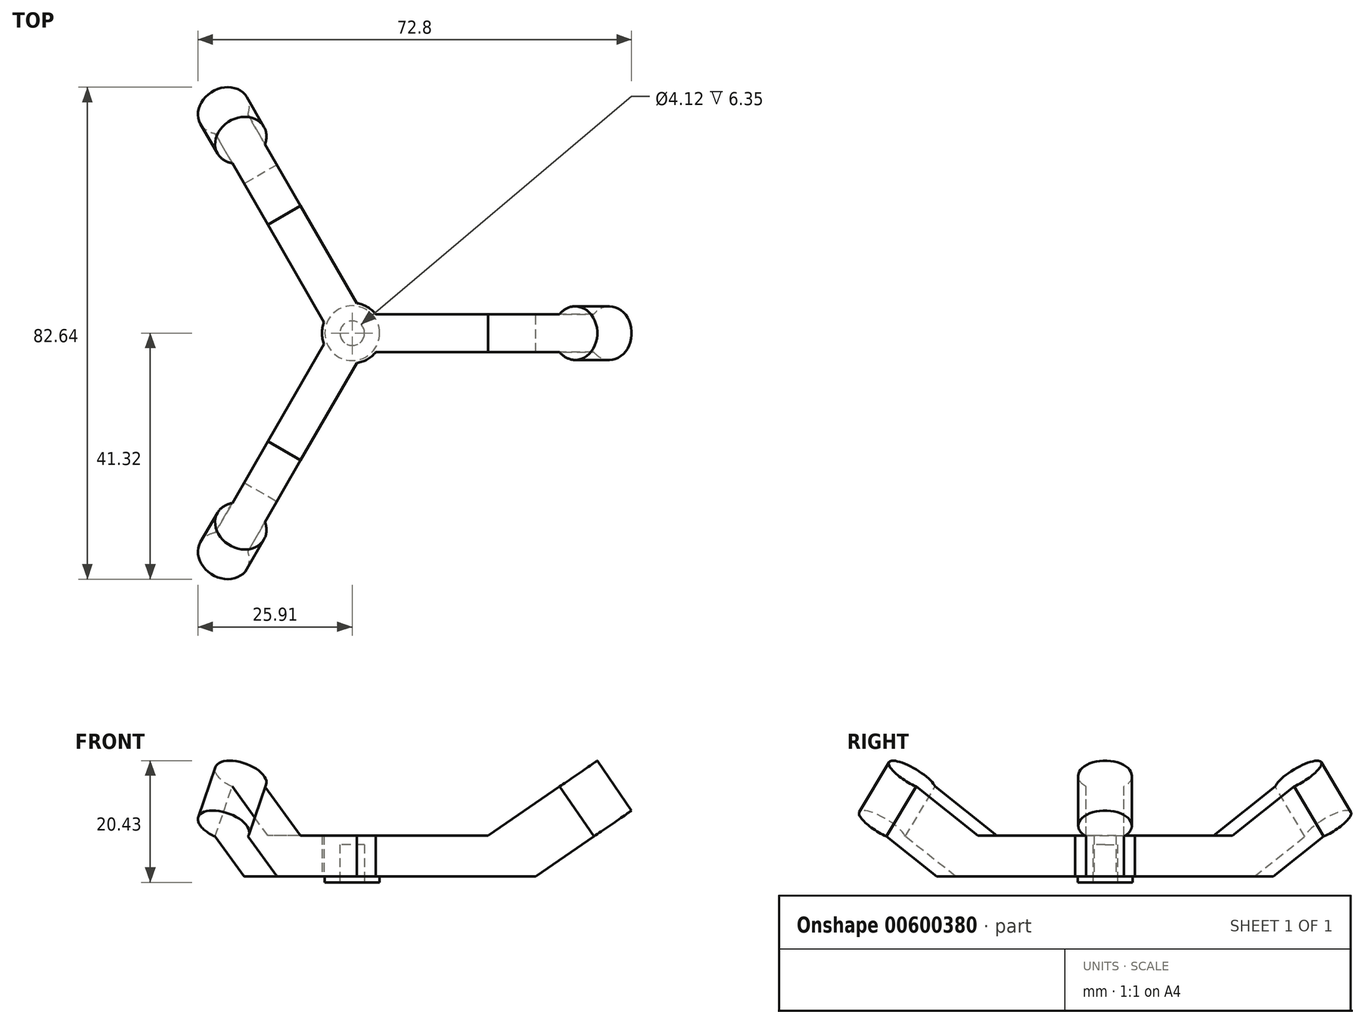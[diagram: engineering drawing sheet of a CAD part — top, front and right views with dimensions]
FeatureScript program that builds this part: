
annotation { "Feature Type Name" : "Feature", "Feature Type Description" : "" }
export const myFeature = defineFeature(function(context is Context, id is Id, definition is map)
    precondition{}
    {
        {
            var Q0;
            Q0=qCreatedBy(makeId("Front.planeOp"),FACE);
            var sketch = newSketch(context, id + "F0", { "sketchPlane" : qUnion([Q0])});
            skCircle(sketch, "E0", {"center": v(0, 59.06) * mm, "radius": 63.5 * mm, "construction": true});
            skCircle(sketch, "E1", {"center": v(38.1, 3.57) * mm, "radius": 5 * mm, "construction": true});
            skLineSegment(sketch, "E2", {"start": v(33.16, 2.82) * mm, "end": v(40.58, 7.9) * mm, "construction": true});
            skLineSegment(sketch, "E3", {"start": v(33.16, 2.82) * mm, "end": v(33.72, 2) * mm, "construction": true});
            skLineSegment(sketch, "E4", {"start": v(33.72, 2) * mm, "end": v(41.14, 7.09) * mm, "construction": true});
            skLineSegment(sketch, "E5", {"start": v(41.14, 7.09) * mm, "end": v(40.58, 7.9) * mm, "construction": true});
            skLineSegment(sketch, "E6", {"start": v(38.1, 3.57) * mm, "end": v(0, 59.06) * mm, "construction": true});
            skLineSegment(sketch, "E7", {"start": v(0, -6.99) * mm, "end": v(2.06, -6.99) * mm});
            skLineSegment(sketch, "E8", {"start": v(2.06, -6.99) * mm, "end": v(2.06, -12.34) * mm});
            skLineSegment(sketch, "E9", {"start": v(0, -6.99) * mm, "end": v(0, -5.49) * mm});
            skLineSegment(sketch, "E10", {"start": v(0, -5.49) * mm, "end": v(22.83, -5.49) * mm});
            skLineSegment(sketch, "E11", {"start": v(22.83, -5.49) * mm, "end": v(33.72, 2) * mm});
            skLineSegment(sketch, "E12", {"start": v(33.72, 2) * mm, "end": v(41.14, 7.09) * mm});
            skLineSegment(sketch, "E13", {"start": v(2.06, -12.34) * mm, "end": v(30.8, -12.33) * mm});
            skLineSegment(sketch, "E14", {"start": v(30.8, -12.33) * mm, "end": v(46.9, -1.3) * mm});
            skLineSegment(sketch, "E15", {"start": v(46.9, -1.3) * mm, "end": v(41.14, 7.09) * mm});
            skLineSegment(sketch, "E16", {"start": v(0, 0) * mm, "end": v(0, -5.49) * mm, "construction": true});
            skSolve(sketch);
        }
        {
            var Q0;
            Q0=qSketchRegion(id+"F0",true);
            extrude(context, id + "F1", {"entities" : qUnion([Q0]), "endBound" : BoundingType.SYMMETRIC, "depth" : 6.35 * mm, "offsetDistance" : 25.4 * mm});
        }
        {
            var Q0;
            Q0=makeQuery(id+"F1.opExtrude","SWEPT_FACE",FACE,{"disambiguationData":[OSD([sQuery(id+"F0.wireOp",EDGE,"E11"),sQuery(id+"F0.wireOp",EDGE,"E12")])]});
            var sketch = newSketch(context, id + "F2", { "sketchPlane" : qUnion([Q0])});
            skLineSegment(sketch, "E17.0", {"start": v(37.93, -3.18) * mm, "end": v(37.93, 3.17) * mm});
            skLineSegment(sketch, "E18.0", {"start": v(15.72, 3.18) * mm, "end": v(37.93, 3.18) * mm});
            skLineSegment(sketch, "E19.0", {"start": v(15.72, -3.18) * mm, "end": v(37.93, -3.18) * mm});
            skCircle(sketch, "E20", {"center": v(33.43, 0) * mm, "radius": 4.5 * mm});
            skSolve(sketch);
        }
        {
            var Q0;
            {var subQ0=sQuery(id+"F2.wireOp",EDGE,"E20");var subQ1=sQuery(id+"F2.wireOp",EDGE,"E18.0");var subQ2=makeQuery(id+"F2.imprint","INTERSECT",VERTEX,{"disambiguationData":[OD(0.0)],"derivedFrom":[subQ1,subQ0]});Q0=makeQuery(id+"F2.imprint","IMPRINT",FACE,{"disambiguationData":[TD([[makeQuery(id+"F2.imprint","IMPRINT",EDGE,{"disambiguationData":[TD([[subQ2,-1.0]])],"derivedFrom":subQ1}),1.0]])]});}
            var Q1;
            {var subQ0=sQuery(id+"F2.wireOp",EDGE,"E20");var subQ1=sQuery(id+"F2.wireOp",EDGE,"E19.0");var subQ2=makeQuery(id+"F2.imprint","INTERSECT",VERTEX,{"disambiguationData":[OD(0.0)],"derivedFrom":[subQ1,subQ0]});Q1=makeQuery(id+"F2.imprint","IMPRINT",FACE,{"disambiguationData":[TD([[makeQuery(id+"F2.imprint","IMPRINT",EDGE,{"disambiguationData":[TD([[subQ2,-1.0]])],"derivedFrom":subQ1}),-1.0]])]});}
            var Q2;
            {var subQ0=sQuery(id+"F2.wireOp",EDGE,"E20");var subQ1=sQuery(id+"F2.wireOp",EDGE,"E18.0");var subQ2=makeQuery(id+"F2.imprint","INTERSECT",VERTEX,{"disambiguationData":[OD(0.0)],"derivedFrom":[subQ1,subQ0]});Q2=makeQuery(id+"F2.imprint","IMPRINT",FACE,{"disambiguationData":[TD([[makeQuery(id+"F2.imprint","IMPRINT",EDGE,{"disambiguationData":[TD([[subQ2,-1.0]])],"derivedFrom":subQ1}),-1.0]])]});}
            var Q3;
            Q3=makeQuery(id+"F1.opExtrude","SWEPT_FACE",FACE,{"disambiguationData":[OSD([sQuery(id+"F0.wireOp",EDGE,"E14")])]});
            extrude(context, id + "F3", {"entities" : qUnion([Q0, Q1, Q2]), "operationType" : NewBodyOperationType.ADD, "endBound" : BoundingType.UP_TO_SURFACE, "oppositeDirection" : true, "depth" : 25.4 * mm, "endBoundEntityFace" : qUnion([Q3]), "offsetDistance" : 25.4 * mm});
        }
        {
            var Q0;
            Q0=makeQuery(id+"F3.boolean.opBoolean","MERGE",FACE,{"derivedFrom":[makeQuery(id+"F1.opExtrude","SWEPT_FACE",FACE,{"disambiguationData":[OSD([sQuery(id+"F0.wireOp",EDGE,"E11"),sQuery(id+"F0.wireOp",EDGE,"E12")])]}),makeQuery(id+"F3.opExtrude","CAP_FACE",FACE,{"disambiguationData":[OSD([sQuery(id+"F2.wireOp",EDGE,"E20")])],"isStart":true})]});
            var sketch = newSketch(context, id + "F4", { "sketchPlane" : qUnion([Q0])});
            skLineSegment(sketch, "E21.0.0", {"start": v(37.93, -3.18) * mm, "end": v(37.93, 3.17) * mm});
            skLineSegment(sketch, "E21.0.1", {"start": v(37.93, 3.18) * mm, "end": v(36.62, 3.18) * mm});
            skArc(sketch, "E21.0.2", {"start": v(36.62, 3.17) * mm, "mid": v(33.43, 4.5) * mm, "end": v(30.24, 3.18) * mm});
            skLineSegment(sketch, "E21.0.3", {"start": v(30.24, 3.18) * mm, "end": v(15.72, 3.18) * mm});
            skLineSegment(sketch, "E21.0.4", {"start": v(15.72, 3.17) * mm, "end": v(15.72, -3.18) * mm});
            skLineSegment(sketch, "E21.0.5", {"start": v(15.72, -3.18) * mm, "end": v(30.24, -3.18) * mm});
            skArc(sketch, "E21.0.6", {"start": v(30.24, -3.18) * mm, "mid": v(33.43, -4.5) * mm, "end": v(36.62, -3.17) * mm});
            skLineSegment(sketch, "E21.0.7", {"start": v(36.62, -3.18) * mm, "end": v(37.93, -3.18) * mm});
            skCircle(sketch, "E22", {"center": v(33.43, 0) * mm, "radius": 4.5 * mm});
            skSolve(sketch);
        }
        {
            var Q0;
            {var subQ0=sQuery(id+"F4.wireOp",EDGE,"E21.0.7");Q0=makeQuery(id+"F4.imprint","IMPRINT",FACE,{"disambiguationData":[TD([[makeQuery(id+"F4.imprint","IMPRINT",EDGE,{"derivedFrom":subQ0}),1.0]])]});}
            var Q1;
            {var subQ0=sQuery(id+"F4.wireOp",EDGE,"E21.0.1");Q1=makeQuery(id+"F4.imprint","IMPRINT",FACE,{"disambiguationData":[TD([[makeQuery(id+"F4.imprint","IMPRINT",EDGE,{"derivedFrom":subQ0}),-1.0]])]});}
            extrude(context, id + "F5", {"entities" : qUnion([Q0, Q1]), "operationType" : NewBodyOperationType.REMOVE, "endBound" : BoundingType.THROUGH_ALL, "oppositeDirection" : true, "depth" : 25.4 * mm, "offsetDistance" : 25.4 * mm});
        }
        {
            var Q0;
            Q0=makeQuery(id+"F1.opExtrude","SWEPT_BODY",BODY,{"disambiguationData":[OSD([sQuery(id+"F0.wireOp",EDGE,"E7"),sQuery(id+"F0.wireOp",EDGE,"E8"),sQuery(id+"F0.wireOp",EDGE,"E9"),sQuery(id+"F0.wireOp",EDGE,"E10"),sQuery(id+"F0.wireOp",EDGE,"E11"),sQuery(id+"F0.wireOp",EDGE,"E12"),sQuery(id+"F0.wireOp",EDGE,"E13"),sQuery(id+"F0.wireOp",EDGE,"E14"),sQuery(id+"F0.wireOp",EDGE,"E15")])]});
            var Q1;
            Q1=sQuery(id+"F0.wireOp",EDGE,"E16");
            circularPattern(context, id + "F6", {"operationType" : NewBodyOperationType.ADD, "entities" : qUnion([Q0]), "axis" : qUnion([Q1]), "angle" : 360 * degree, "instanceCount" : 3, "equalSpace" : true});
        }
        {
            var Q0;
            Q0=makeQuery(id+"F1.opExtrude","SWEPT_FACE",FACE,{"disambiguationData":[OSD([sQuery(id+"F0.wireOp",EDGE,"E13")])]});
            var sketch = newSketch(context, id + "F7", { "sketchPlane" : qUnion([Q0])});
            skCircle(sketch, "E23", {"center": v(0, 0) * mm, "radius": 2.06 * mm});
            skLineSegment(sketch, "E24.0.0", {"start": v(1.72, 3.37) * mm, "end": v(-12.65, 28.27) * mm});
            skLineSegment(sketch, "E24.0.1", {"start": v(-12.65, 28.27) * mm, "end": v(-18.15, 25.1) * mm});
            skLineSegment(sketch, "E24.0.2", {"start": v(-18.15, 25.1) * mm, "end": v(-3.78, 0.2) * mm});
            skLineSegment(sketch, "E24.0.3", {"start": v(-3.78, 0.2) * mm, "end": v(1.72, 3.37) * mm});
            skCircle(sketch, "E25", {"center": v(0, 0) * mm, "radius": 5.08 * mm});
            skSolve(sketch);
        }
        {
            var Q0;
            {var subQ0=sQuery(id+"F7.wireOp",EDGE,"E24.0.3");var subQ1=sQuery(id+"F7.wireOp",EDGE,"E23");var subQ2=makeQuery(id+"F7.imprint","INTERSECT",VERTEX,{"derivedFrom":[subQ1,subQ0]});Q0=makeQuery(id+"F7.imprint","IMPRINT",FACE,{"disambiguationData":[TD([[makeQuery(id+"F7.imprint","IMPRINT",EDGE,{"disambiguationData":[TD([[subQ2,1.0]])],"derivedFrom":subQ1}),-1.0]])]});}
            var Q1;
            {var subQ0=sQuery(id+"F7.wireOp",EDGE,"E24.0.3");var subQ1=sQuery(id+"F7.wireOp",EDGE,"E23");var subQ2=makeQuery(id+"F7.imprint","INTERSECT",VERTEX,{"derivedFrom":[subQ1,subQ0]});Q1=makeQuery(id+"F7.imprint","IMPRINT",FACE,{"disambiguationData":[TD([[makeQuery(id+"F7.imprint","IMPRINT",EDGE,{"disambiguationData":[TD([[subQ2,-1.0]])],"derivedFrom":subQ1}),-1.0]])]});}
            var Q2;
            {var subQ0=makeQuery(id+"F1.opExtrude","SWEPT_FACE",FACE,{"disambiguationData":[OSD([sQuery(id+"F0.wireOp",EDGE,"E10")])]});Q2=makeQuery(id+"F6.boolean.opBoolean","MERGE",FACE,{"derivedFrom":[subQ0,makeQuery(id+"F6.opPattern","COPY",FACE,{"derivedFrom":subQ0,"instanceName":"1"}),makeQuery(id+"F6.opPattern","COPY",FACE,{"derivedFrom":subQ0,"instanceName":"2"})]});}
            extrude(context, id + "F8", {"entities" : qUnion([Q0, Q1]), "operationType" : NewBodyOperationType.ADD, "endBound" : BoundingType.UP_TO_SURFACE, "oppositeDirection" : true, "depth" : 25.4 * mm, "endBoundEntityFace" : qUnion([Q2]), "offsetDistance" : 25.4 * mm});
        }
        {
            var Q0;
            {var subQ0=sQuery(id+"F7.wireOp",EDGE,"E25");var subQ1=sQuery(id+"F7.wireOp",EDGE,"E24.0.3");var subQ2=sQuery(id+"F7.wireOp",EDGE,"E23");var subQ3=sQuery(id+"F0.wireOp",EDGE,"E13");var subQ4=sQuery(id+"F0.wireOp",EDGE,"E8");var subQ5=makeQuery(id+"F1.opExtrude","SWEPT_FACE",FACE,{"disambiguationData":[OSD([subQ3])]});Q0=makeQuery(id+"F8.boolean.opBoolean","MERGE",FACE,{"derivedFrom":[subQ5,makeQuery(id+"F6.opPattern","COPY",FACE,{"derivedFrom":subQ5,"instanceName":"1"}),makeQuery(id+"F6.opPattern","COPY",FACE,{"derivedFrom":subQ5,"instanceName":"2"}),makeQuery(id+"F8.opExtrude","CAP_FACE",FACE,{"disambiguationData":[OSD([subQ4,subQ3,subQ2,sQuery(id+"F7.wireOp",EDGE,"E24.0.0"),subQ1,subQ0])],"isStart":true}),makeQuery(id+"F8.opExtrude","CAP_FACE",FACE,{"disambiguationData":[OSD([subQ4,subQ3,subQ2,sQuery(id+"F7.wireOp",EDGE,"E24.0.2"),subQ1,subQ0])],"isStart":true})]});}
            var sketch = newSketch(context, id + "F9", { "sketchPlane" : qUnion([Q0])});
            skCircle(sketch, "E26.0.0", {"center": v(0, 0) * mm, "radius": 2.06 * mm});
            skCircle(sketch, "E27", {"center": v(0, 0) * mm, "radius": 4.6 * mm});
            skSolve(sketch);
        }
        {
            var Q0;
            Q0 = qSketchRegion(id + "F9", true);
            extrude(context, id + "F10", {"entities" : qUnion([Q0]), "operationType" : NewBodyOperationType.ADD, "depth" : 1 * mm, "offsetDistance" : 25.4 * mm});
        }
    });
